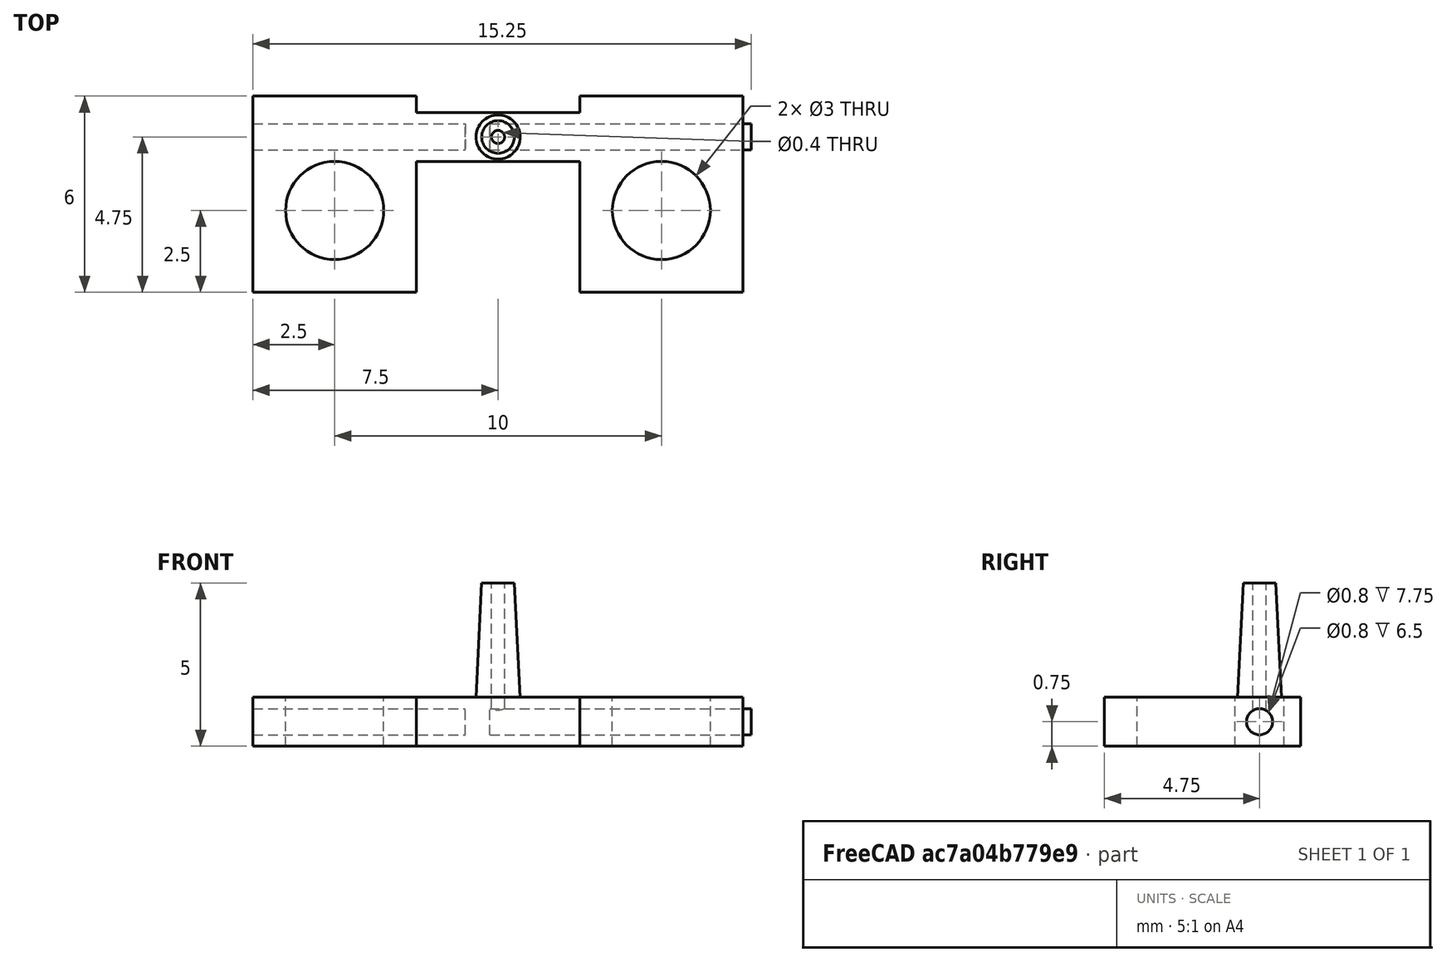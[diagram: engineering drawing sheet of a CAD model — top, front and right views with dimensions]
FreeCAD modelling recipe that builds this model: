
FCSTD DOCUMENT  (FreeCAD 0.17R13509 (Git))
Label: bowtie_2
License: All rights reserved
LicenseURL: http://en.wikipedia.org/wiki/All_rights_reserved
objects: Part::Cylinder×6, Part::Box×3, Part::MultiFuse×2, Part::Cone×1, Part::Cut×1
note: 13 computed .brp shape members not serialized (recipe doc carries the construction recipe); baked Part::Feature solids carry a one-line shape summary decoded from their .brp

FEATURE [Part::Cylinder] Cylinder156  label="BowTieInjectorWire003"
  Angle = 360
  AttacherType = Attacher::AttachEngine3D
  Height = 8
  Placement = pos=(105.17,148,64.75) rot=(0,1,0;1.5708rad)
  Radius = 0.4
  expr: Placement.Base.z = 69.75 - 5
  expr: Placement.Base.y = 148.5 - 0.5
  expr: Placement.Base.x = 121.75 - 16.579999999999998
FEATURE [Part::Cylinder] Cylinder136  label="BowTieNozzle004"
  Angle = 360
  AttacherType = Attacher::AttachEngine3D
  Height = 9
  Placement = pos=(122,148.5,69.5) rot=(0,0,1;0rad)
  Radius = 0.2
FEATURE [Part::Cone] Cone001
  Angle = 360
  AttacherType = Attacher::AttachEngine3D
  Height = 4
  Placement = pos=(122,148.5,70) rot=(0,0,1;0rad)
  Radius1 = 0.7
  Radius2 = 0.5
FEATURE [Part::Cylinder] Cylinder138  label="BowTieInjectorWire1"
  Angle = 360
  AttacherType = Attacher::AttachEngine3D
  Height = 8
  Placement = pos=(121.75,148.5,69.75) rot=(0,1,0;1.5708rad)
  Radius = 0.4
FEATURE [Part::Box] Box026  label="Cube009"
  AttacherType = Attacher::AttachEngine3D
  Height = 1.5
  Length = 5
  Placement = pos=(119.5,147.75,69) rot=(0,0,1;0rad)
  Width = 1.5
FEATURE [Part::Cylinder] Cylinder139  label="BowTieInjectorWire002"
  Angle = 360
  AttacherType = Attacher::AttachEngine3D
  Height = 10
  Placement = pos=(111,148.5,69.75) rot=(0,1,0;1.5708rad)
  Radius = 0.4
FEATURE [Part::Box] Box027  label="Cube010"
  AttacherType = Attacher::AttachEngine3D
  Height = 1.5
  Length = 5
  Placement = pos=(124.5,143.75,69) rot=(0,0,1;0rad)
  Width = 6
FEATURE [Part::Cylinder] Cylinder140  label="BowTieMount003"
  Angle = 360
  AttacherType = Attacher::AttachEngine3D
  Height = 8
  Placement = pos=(127,146.25,63) rot=(0,0,1;0rad)
  Radius = 1.5
  expr: Radius = 3 / 2
FEATURE [Part::Box] Box028  label="Cube011"
  AttacherType = Attacher::AttachEngine3D
  Height = 1.5
  Length = 5
  Placement = pos=(114.5,143.75,69) rot=(0,0,1;0rad)
  Width = 6
FEATURE [Part::Cylinder] Cylinder141  label="BowTieMount004"
  Angle = 360
  AttacherType = Attacher::AttachEngine3D
  Height = 8
  Placement = pos=(117,146.25,63) rot=(0,0,1;0rad)
  Radius = 1.5
  expr: Radius = 3 / 2
FEATURE [Part::MultiFuse] Fusion055  label="BowTieCut"
  Shapes = -> [Cylinder141,Cylinder140,Cylinder138,Cylinder139,Cylinder136]
FEATURE [Part::MultiFuse] Fusion056
  Shapes = -> [Box026,Cone001,Box028,Box027]
FEATURE [Part::Cut] Cut018  label="BowTie"
  Base = -> Fusion056
  Placement = pos=(-16.58,-0.5,-5) rot=(0,0,1;0rad)
  Tool = -> Fusion055
  expr: Placement.Base.x = -40.829999999999998 + 63.5 / 2 - 15 / 2
